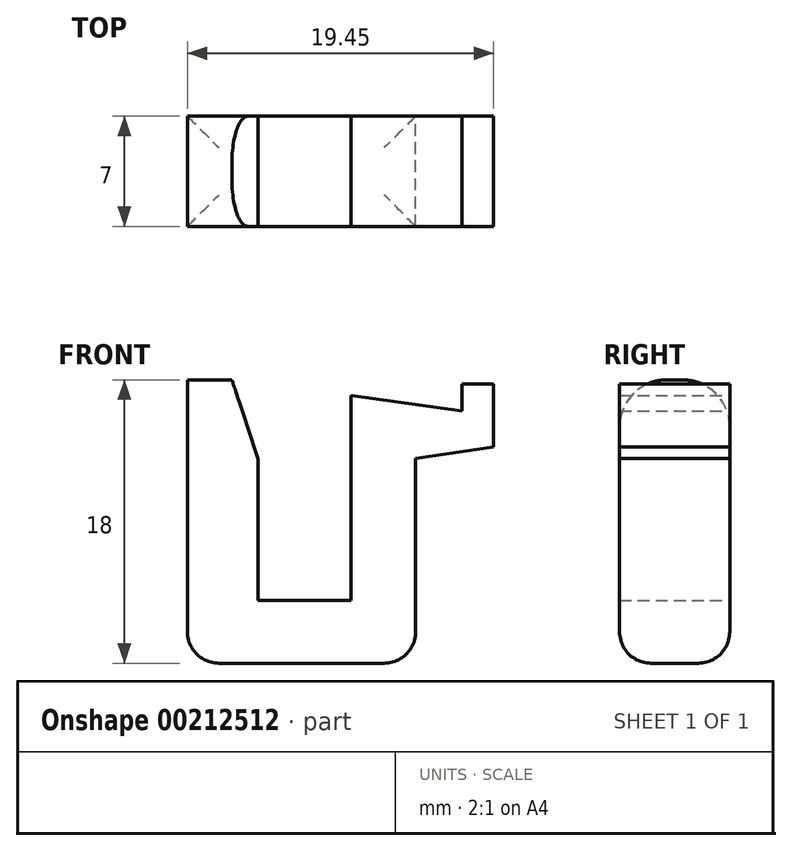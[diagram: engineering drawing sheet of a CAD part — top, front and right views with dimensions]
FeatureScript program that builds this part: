
annotation { "Feature Type Name" : "Feature", "Feature Type Description" : "" }
export const myFeature = defineFeature(function(context is Context, id is Id, definition is map)
    precondition{}
    {
        {
            var Q0;
            Q0=qCreatedBy(makeId("Front.planeOp"),FACE);
            var sketch = newSketch(context, id + "F0", { "sketchPlane" : qUnion([Q0])});
            skLineSegment(sketch, "E0", {"start": v(-12.27, -8.97) * mm, "end": v(-12.27, 0) * mm});
            skLineSegment(sketch, "E1", {"start": v(-16.77, 0.03) * mm, "end": v(-16.77, -12.97) * mm});
            skLineSegment(sketch, "E2", {"start": v(-16.77, -12.97) * mm, "end": v(-2.27, -12.97) * mm});
            skLineSegment(sketch, "E3", {"start": v(-2.27, -12.97) * mm, "end": v(-2.27, -3.97) * mm});
            skLineSegment(sketch, "E4", {"start": v(-6.37, 0.03) * mm, "end": v(-6.37, -8.97) * mm});
            skLineSegment(sketch, "E5", {"start": v(-6.37, -8.97) * mm, "end": v(-12.27, -8.97) * mm});
            skLineSegment(sketch, "E6", {"start": v(-15.62, 5.03) * mm, "end": v(-13.94, 5.03) * mm});
            skLineSegment(sketch, "E7", {"start": v(-16.77, 0.03) * mm, "end": v(-16.77, 5.03) * mm});
            skLineSegment(sketch, "E8", {"start": v(-15.62, 5.03) * mm, "end": v(-16.77, 5.03) * mm});
            skLineSegment(sketch, "E9", {"start": v(-6.37, 0.03) * mm, "end": v(-6.37, 4.03) * mm});
            skLineSegment(sketch, "E10", {"start": v(-6.37, 4.03) * mm, "end": v(0.67, 3.05) * mm});
            skLineSegment(sketch, "E11", {"start": v(2.67, 2.77) * mm, "end": v(2.68, 0.77) * mm});
            skLineSegment(sketch, "E12", {"start": v(-2.27, -3.97) * mm, "end": v(-2.27, 0.03) * mm});
            skLineSegment(sketch, "E13", {"start": v(2.68, 0.77) * mm, "end": v(-2.27, 0.03) * mm});
            skLineSegment(sketch, "E14", {"start": v(2.67, 2.77) * mm, "end": v(2.67, 4.77) * mm});
            skLineSegment(sketch, "E15", {"start": v(2.67, 4.77) * mm, "end": v(0.67, 4.77) * mm});
            skLineSegment(sketch, "E16", {"start": v(0.67, 4.77) * mm, "end": v(0.67, 3.05) * mm});
            skLineSegment(sketch, "E17", {"start": v(-13.94, 5.03) * mm, "end": v(-12.27, 0) * mm});
            skPoint(sketch, "E18.orphan", {"position": v(-12.27, 5.03) * mm});
            skSolve(sketch);
        }
        {
            var Q0;
            Q0=makeQuery(id+"F0.imprint","IMPRINT",FACE,{"disambiguationData":[TD([[makeQuery(id+"F0.imprint","IMPRINT",EDGE,{"derivedFrom":sQuery(id+"F0.wireOp",EDGE,"E0")}),1.0]])]});
            extrude(context, id + "F1", {"entities" : qUnion([Q0]), "endBound" : BoundingType.SYMMETRIC, "depth" : 7 * mm});
        }
        {
            var Q0;
            Q0=makeQuery(id+"F1.opExtrude","CAP_EDGE",EDGE,{"disambiguationData":[OSD([sQuery(id+"F0.wireOp",EDGE,"E6"),sQuery(id+"F0.wireOp",EDGE,"E8")])],"isStart":true});
            var Q1;
            Q1=makeQuery(id+"F1.opExtrude","CAP_EDGE",EDGE,{"disambiguationData":[OSD([sQuery(id+"F0.wireOp",EDGE,"E6"),sQuery(id+"F0.wireOp",EDGE,"E8")])],"isStart":false});
            fillet(context, id + "F2", {"entities" : qUnion([Q0, Q1]), "radius" : 3 * mm, "tangentPropagation" : true, "allowEdgeOverflow" : false});
        }
        {
            var Q0;
            Q0=makeQuery(id+"F2.opFillet","BLEND_EDGE",EDGE,{"blendedFrom":[makeQuery(id+"F1.opExtrude","CAP_EDGE",EDGE,{"disambiguationData":[OSD([sQuery(id+"F0.wireOp",EDGE,"E6"),sQuery(id+"F0.wireOp",EDGE,"E8")])],"isStart":true}),makeQuery(id+"F1.opExtrude","SWEPT_FACE",FACE,{"disambiguationData":[OSD([sQuery(id+"F0.wireOp",EDGE,"E0")])]})],"blendedInto":[makeQuery(id+"F1.opExtrude","SWEPT_FACE",FACE,{"disambiguationData":[OSD([sQuery(id+"F0.wireOp",EDGE,"E0")])]})]});
            var Q1;
            Q1=makeQuery(id+"F1.opExtrude","SWEPT_FACE",FACE,{"disambiguationData":[OSD([sQuery(id+"F0.wireOp",EDGE,"E2")])]});
            fillet(context, id + "F3", {"entities" : qUnion([Q0, Q1]), "radius" : 2 * mm, "tangentPropagation" : true, "allowEdgeOverflow" : false});
        }
    });
